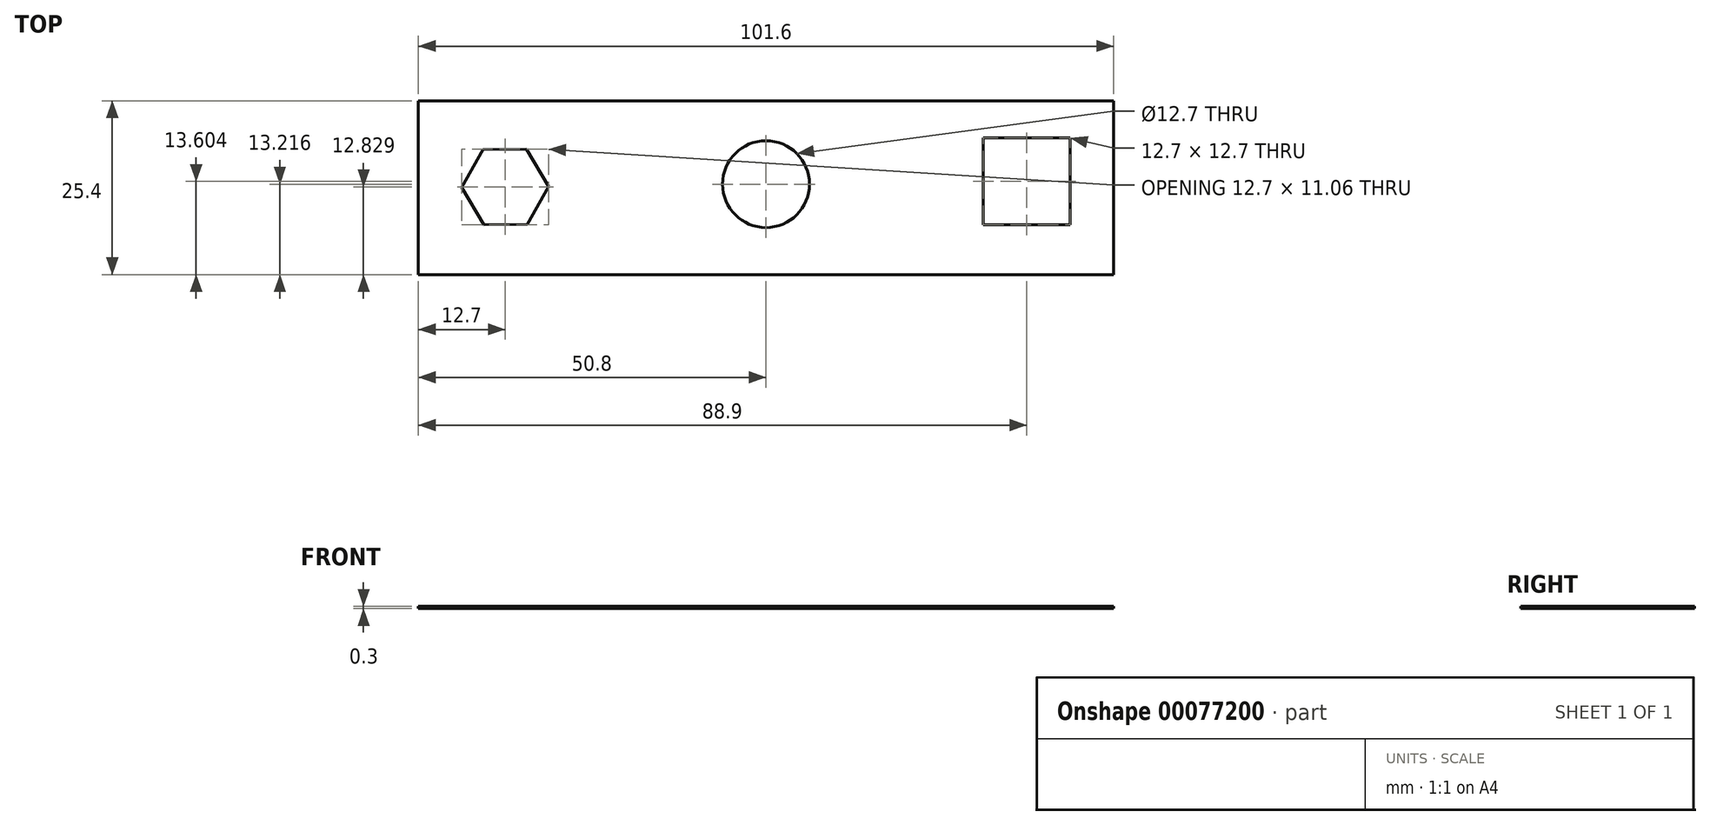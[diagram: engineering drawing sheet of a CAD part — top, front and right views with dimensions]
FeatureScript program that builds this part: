
annotation { "Feature Type Name" : "Feature", "Feature Type Description" : "" }
export const myFeature = defineFeature(function(context is Context, id is Id, definition is map)
    precondition{}
    {
        {
            var Q0;
            Q0=qCreatedBy(makeId("Top.planeOp"),FACE);
            var sketch = newSketch(context, id + "F0", { "sketchPlane" : qUnion([Q0])});
            skLineSegment(sketch, "E0.bottom", {"start": v(0, 0) * mm, "end": v(101.6, 0) * mm});
            skLineSegment(sketch, "E0.top", {"start": v(0, 25.4) * mm, "end": v(101.6, 25.4) * mm});
            skLineSegment(sketch, "E0.left", {"start": v(0, 0) * mm, "end": v(0, 25.4) * mm});
            skLineSegment(sketch, "E0.right", {"start": v(101.6, 0) * mm, "end": v(101.6, 25.4) * mm});
            skCircle(sketch, "E1", {"center": v(12.7, 12.83) * mm, "radius": 6.35 * mm, "construction": true});
            skLineSegment(sketch, "E2", {"start": v(0, 12.7) * mm, "end": v(101.6, 13.73) * mm, "construction": true});
            skLineSegment(sketch, "E3.0", {"start": v(15.82, 18.36) * mm, "end": v(19.05, 12.9) * mm});
            skLineSegment(sketch, "E3.1", {"start": v(19.05, 12.9) * mm, "end": v(15.93, 7.36) * mm});
            skLineSegment(sketch, "E3.2", {"start": v(15.93, 7.36) * mm, "end": v(9.58, 7.3) * mm});
            skLineSegment(sketch, "E3.3", {"start": v(9.58, 7.3) * mm, "end": v(6.35, 12.76) * mm});
            skLineSegment(sketch, "E3.4", {"start": v(6.35, 12.76) * mm, "end": v(9.47, 18.3) * mm});
            skLineSegment(sketch, "E3.5", {"start": v(9.47, 18.3) * mm, "end": v(15.82, 18.36) * mm});
            skCircle(sketch, "E4", {"center": v(50.8, 13.22) * mm, "radius": 6.35 * mm});
            skLineSegment(sketch, "E5.bottom", {"start": v(95.25, 19.95) * mm, "end": v(82.55, 19.95) * mm});
            skLineSegment(sketch, "E5.top", {"start": v(95.25, 7.25) * mm, "end": v(82.55, 7.25) * mm});
            skLineSegment(sketch, "E5.left", {"start": v(95.25, 19.95) * mm, "end": v(95.25, 7.25) * mm});
            skLineSegment(sketch, "E5.right", {"start": v(82.55, 19.95) * mm, "end": v(82.55, 7.25) * mm});
            skPoint(sketch, "E5.middle", {"position": v(88.9, 13.6) * mm});
            skSolve(sketch);
        }
        {
            var Q0;
            Q0=makeQuery(id+"F0.imprint","IMPRINT",FACE,{"disambiguationData":[TD([[makeQuery(id+"F0.imprint","IMPRINT",EDGE,{"derivedFrom":sQuery(id+"F0.wireOp",EDGE,"E0.bottom")}),1.0]])]});
            extrude(context, id + "F1", {"entities" : qUnion([Q0]), "depth" : .3 * mm});
        }
    });
